# Revit family: RRPVCZNC
name_source: partatom
category: Generic Models
revit_build: Autodesk Revit 2018 (Build: 20190510_1515(x64)
units: mm (PartAtom-declared; Revit-internal decimal feet)

## family parameters
Always vertical = Yes
Can host rebar = No
Cut with Voids When Loaded = No
Part Type = Normal
Room Calculation Point = No
Round Connector Dimension = Use Diameter
Shared = Yes
Work Plane-Based = Yes

## types (9) — shared parameters
Default Elevation = 48 "
Patent Information = 10495237, 10,697,562, 10,844,978, 11,262,000
Rod Material = <By Category>

## per-type parameters (varying)
| type | Description | Rod Cut Length | Rod Radius | Rod Size |
| RRPVCZNC061/2 | Threaded Rod 1/2 Inch Steel 6 Foot long Zinc Plated w/FDA Compliant PVC Encasement | 72 " | 0.25 " | 0.5 " |
| RRPVCZNC063/8 | Threaded Rod 3/8 Inch Steel 6 Foot long Zinc Plated w/FDA Compliant PVC Encasement | 72 " | 0.188 " | 0.375 " |
| RRPVCZNC061/4 | Threaded Rod 1/4 Inch Steel 6 Foot long Zinc Plated PVC Encasement | 72 " | 0.125 " | 0.25 " |
| RRPVCZNC065/8 | Threaded Rod 5/8 Inch Steel 6 Foot long Zinc Plated w/FDA Compliant PVC Encasement | 72 " | 0.313 " | 0.625 " |
| RRPVCZNC063/4 | Threaded Rod 3/4 Inch Steel 6 Foot long Zinc Plated w/FDA Compliant PVC Encasement | 72 " | 0.375 " | 0.75 " |
| RRPVCZNC123/8 | Threaded Rod 3/8 Inch Steel 12 Foot long Zinc Plated w/FDA Compliant PVC Encasement | 144 " | 0.188 " | 0.375 " |
| RRPVCZNC121/2 | Threaded Rod 1/2 Inch Steel 12 Foot long Zinc Plated w/FDA Compliant PVC Encasement | 144 " | 0.25 " | 0.5 " |
| RRPVCZNC125/8 | Threaded Rod 5/8 Inch Steel 12 Foot long Zinc Plated w/FDA Compliant PVC Encasement | 144 " | 0.313 " | 0.625 " |
| RRPVCZNC123/4 | Threaded Rod 3/4 Inch Steel 12 Foot long Zinc Plated w/FDA Compliant PVC Encasement | 144 " | 0.375 " | 0.75 " |

note: column(s) folded — value = type name in every type: Catalog Number

## geometry (parser evidence)
native form markers: Sweep x3
no freeform markers — native parametric forms only
